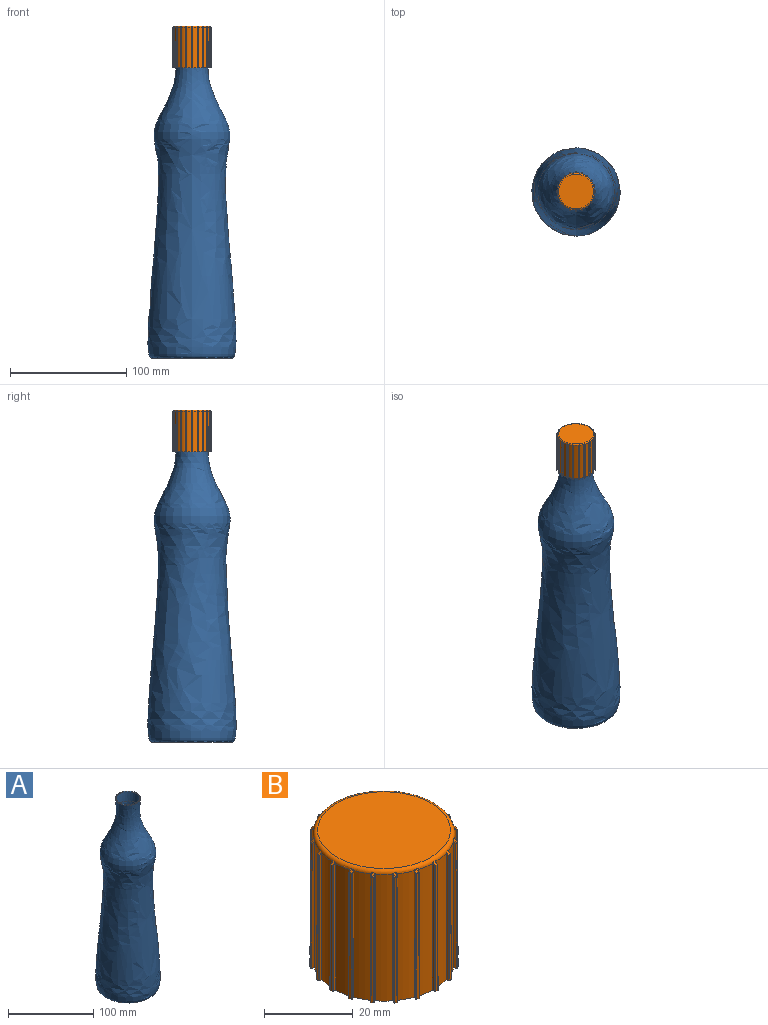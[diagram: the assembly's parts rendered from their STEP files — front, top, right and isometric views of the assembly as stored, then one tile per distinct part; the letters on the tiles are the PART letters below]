
ASSEMBLY  parts=2 mates=1
PART A: 4 faces, bbox 76x76x269.3 mm
  f0: revolved ~269.25x75.99mm, area 54828.4mm2, adj f3
  f1: revolved ~252.83x70.44mm, area 48526.9mm2, adj f2
  f2: cone r=13.64mm half-angle=3.7deg, axis (0,0,1), area 1081.3mm2, adj f1,f3
  f3: plane 29.42x29.42mm, normal (0,0,1), area 95.4mm2, adj f0,f2
PART B: 267 faces, bbox 35.1x35.1x36 mm
  f0: cylinder r=16mm len=35mm, axis (0,0,1), area 140.9mm2, adj f19,f25,f88,f255
  f1: cylinder r=16mm len=35mm, axis (0,0,1), area 140.9mm2, adj f19,f25,f160,f243
  f2: cylinder r=16mm len=35mm, axis (0,0,1), area 140.9mm2, adj f19,f25,f112,f231
  f3: cylinder r=16mm len=35mm, axis (0,0,1), area 140.9mm2, adj f19,f25,f76,f219
  f4: cylinder r=16mm len=35mm, axis (0,0,1), area 140.9mm2, adj f19,f25,f52,f207
  f5: cylinder r=16mm len=35mm, axis (0,0,1), area 140.9mm2, adj f19,f25,f64,f195
  f6: cylinder r=16mm len=35mm, axis (0,0,1), area 140.9mm2, adj f19,f21,f25,f183
  f7: cylinder r=16mm len=35mm, axis (0,0,1), area 140.9mm2, adj f19,f25,f171,f184
  f8: cylinder r=16mm len=35mm, axis (0,0,1), area 140.9mm2, adj f19,f25,f136,f159
  f9: cylinder r=16mm len=35mm, axis (0,0,1), area 140.9mm2, adj f19,f25,f147,f208
  f10: cylinder r=16mm len=35mm, axis (0,0,1), area 140.9mm2, adj f19,f25,f100,f135
  f11: cylinder r=16mm len=35mm, axis (0,0,1), area 140.9mm2, adj f19,f25,f40,f123
  f12: cylinder r=16mm len=35mm, axis (0,0,1), area 140.9mm2, adj f19,f25,f111,f244
  f13: cylinder r=16mm len=35mm, axis (0,0,1), area 140.9mm2, adj f19,f25,f99,f256
  f14: cylinder r=16mm len=35mm, axis (0,0,1), area 140.9mm2, adj f19,f25,f87,f148
  f15: cylinder r=16mm len=35mm, axis (0,0,1), area 140.9mm2, adj f19,f25,f75,f172
  f16: cylinder r=16mm len=35mm, axis (0,0,1), area 140.9mm2, adj f19,f25,f63,f124
  f17: cylinder r=16mm len=35mm, axis (0,0,1), area 140.9mm2, adj f19,f25,f51,f220
  f18: cylinder r=16mm len=35mm, axis (0,0,1), area 140.9mm2, adj f19,f25,f39,f232
  f19: torus R=15mm, axis (0,0,1), area 148.2mm2, adj f0,f1,f2,f3,f4,f5,f6,f7
  f20: plane 35.03x0.66mm, normal (-0.31,-0.95,0), area 21mm2, adj f19,f22,f25,f28,f33
  f21: plane 35.03x0.66mm, normal (0.31,0.95,0), area 21mm2, adj f6,f19,f24,f25,f29
  f22: cylinder r=0.2mm len=0.82mm, axis (-0.67,0.22,-0.71), area 0.3mm2, adj f19,f20,f23,f27,f31
  f23: cylinder r=0.2mm len=0.82mm, axis (-0.31,-0.95,0), area 0.1mm2, adj f19,f22,f24,f27
  f24: cylinder r=0.2mm len=0.84mm, axis (-0.67,0.22,-0.71), area 0.3mm2, adj f19,f21,f23,f27,f32
  f25: plane 33.77x33.77mm, normal (0,0,-1), area 66.9mm2, adj f0,f1,f2,f3,f4,f5,f6,f7
  f26: plane 34.53x0.63mm, normal (-0.95,0.31,0.01), area 20.7mm2, adj f25,f28,f29,f30
  f27: plane 0.76x0.76mm, normal (-0.67,0.22,0.71), area 0.5mm2, adj f22,f23,f24,f30
  f28: cylinder r=0.2mm len=34.53mm, axis (-0.01,0,-1), area 10.8mm2, adj f20,f25,f26,f31
  f29: cylinder r=0.2mm len=34.53mm, axis (0.01,0,1), area 10.8mm2, adj f21,f25,f26,f32
  f30: cylinder r=0.2mm len=0.59mm, axis (-0.31,-0.95,0), area 0.1mm2, adj f26,f27,f31,f32
  f31: sphere r=0.2mm, area 0mm2, adj f22,f28,f30
  f32: sphere r=0.2mm, area 0mm2, adj f24,f29,f30
  f33: cylinder r=16mm len=35mm, axis (0,0,1), area 140.9mm2, adj f19,f20,f25,f196
  f34: plane 30x30mm, normal (0,0,1), area 706.9mm2, adj f19
  f35: plane 27x27mm, normal (0,0,-1), area 572.6mm2, adj f36
  f36: torus R=13.5mm, axis (0,0,1), area 139.5mm2, adj f35,f37
  f37: cylinder r=14.5mm len=32.5mm, axis (0,0,1), area 2961mm2, adj f36,f38
  f38: torus R=15.5mm, axis (0,0,1), area 146.7mm2, adj f25,f37
  f39: plane 35.03x0.56mm, normal (0.81,-0.59,0), area 21mm2, adj f18,f19,f25,f41,f46
  f40: plane 35.03x0.56mm, normal (-0.81,0.59,0), area 21mm2, adj f11,f19,f25,f43,f47
  f41: cylinder r=0.2mm len=0.82mm, axis (-0.42,-0.57,-0.71), area 0.3mm2, adj f19,f39,f42,f45,f49
  f42: cylinder r=0.2mm len=0.73mm, axis (0.81,-0.59,0), area 0.1mm2, adj f19,f41,f43,f45
  f43: cylinder r=0.2mm len=0.82mm, axis (-0.42,-0.57,-0.71), area 0.3mm2, adj f19,f40,f42,f45,f50
  f44: plane 34.53x0.59mm, normal (-0.59,-0.81,0.01), area 20.7mm2, adj f25,f46,f47,f48
  f45: plane 0.84x0.84mm, normal (-0.41,-0.57,0.71), area 0.5mm2, adj f41,f42,f43,f48
  f46: cylinder r=0.2mm len=34.53mm, axis (0,0,-1), area 10.8mm2, adj f25,f39,f44,f49
  f47: cylinder r=0.2mm len=34.53mm, axis (0,0,1), area 10.8mm2, adj f25,f40,f44,f50
  f48: cylinder r=0.2mm len=0.52mm, axis (0.81,-0.59,0), area 0.1mm2, adj f44,f45,f49,f50
  f49: sphere r=0.2mm, area 0mm2, adj f41,f46,f48
  f50: sphere r=0.2mm, area 0mm2, adj f43,f47,f48
  f51: plane 35.03x0.66mm, normal (-0.95,0.31,0), area 21mm2, adj f17,f19,f25,f53,f58
  f52: plane 35.03x0.66mm, normal (0.95,-0.31,0), area 21mm2, adj f4,f19,f25,f55,f59
  f53: cylinder r=0.2mm len=0.82mm, axis (0.22,0.67,-0.71), area 0.3mm2, adj f19,f51,f54,f57,f61
  f54: cylinder r=0.2mm len=0.82mm, axis (-0.95,0.31,0), area 0.1mm2, adj f19,f53,f55,f57
  f55: cylinder r=0.2mm len=0.84mm, axis (0.22,0.67,-0.71), area 0.3mm2, adj f19,f52,f54,f57,f62
  f56: plane 34.53x0.63mm, normal (0.31,0.95,0.01), area 20.7mm2, adj f25,f58,f59,f60
  f57: plane 0.76x0.76mm, normal (0.22,0.67,0.71), area 0.5mm2, adj f53,f54,f55,f60
  f58: cylinder r=0.2mm len=34.53mm, axis (0,0.01,-1), area 10.8mm2, adj f25,f51,f56,f61
  f59: cylinder r=0.2mm len=34.53mm, axis (0,-0.01,1), area 10.8mm2, adj f25,f52,f56,f62
  f60: cylinder r=0.2mm len=0.59mm, axis (-0.95,0.31,0), area 0.1mm2, adj f56,f57,f61,f62
  f61: sphere r=0.2mm, area 0mm2, adj f53,f58,f60
  f62: sphere r=0.2mm, area 0mm2, adj f55,f59,f60
  f63: plane 35.03x0.66mm, normal (0.31,-0.95,0), area 21mm2, adj f16,f19,f25,f65,f70
  f64: plane 35.03x0.66mm, normal (-0.31,0.95,0), area 21mm2, adj f5,f19,f25,f67,f71
  f65: cylinder r=0.2mm len=0.84mm, axis (-0.67,-0.22,-0.71), area 0.3mm2, adj f19,f63,f66,f69,f73
  f66: cylinder r=0.2mm len=0.82mm, axis (0.31,-0.95,0), area 0.1mm2, adj f19,f65,f67,f69
  f67: cylinder r=0.2mm len=0.82mm, axis (-0.67,-0.22,-0.71), area 0.3mm2, adj f19,f64,f66,f69,f74
  f68: plane 34.53x0.63mm, normal (-0.95,-0.31,0.01), area 20.7mm2, adj f25,f70,f71,f72
  f69: plane 0.76x0.76mm, normal (-0.67,-0.22,0.71), area 0.5mm2, adj f65,f66,f67,f72
  f70: cylinder r=0.2mm len=34.53mm, axis (-0.01,0,-1), area 10.8mm2, adj f25,f63,f68,f73
  f71: cylinder r=0.2mm len=34.53mm, axis (0.01,0,1), area 10.8mm2, adj f25,f64,f68,f74
  f72: cylinder r=0.2mm len=0.59mm, axis (0.31,-0.95,0), area 0.1mm2, adj f68,f69,f73,f74
  f73: sphere r=0.2mm, area 0mm2, adj f65,f70,f72
  f74: sphere r=0.2mm, area 0mm2, adj f67,f71,f72
  f75: plane 35.03x0.66mm, normal (-0.95,-0.31,0), area 21mm2, adj f15,f19,f25,f77,f82
  f76: plane 35.03x0.66mm, normal (0.95,0.31,0), area 21mm2, adj f3,f19,f25,f79,f83
  f77: cylinder r=0.2mm len=0.84mm, axis (-0.22,0.67,-0.71), area 0.3mm2, adj f19,f75,f78,f81,f85
  f78: cylinder r=0.2mm len=0.82mm, axis (-0.95,-0.31,0), area 0.1mm2, adj f19,f77,f79,f81
  f79: cylinder r=0.2mm len=0.82mm, axis (-0.22,0.67,-0.71), area 0.3mm2, adj f19,f76,f78,f81,f86
  f80: plane 34.53x0.63mm, normal (-0.31,0.95,0.01), area 20.7mm2, adj f25,f82,f83,f84
  f81: plane 0.76x0.76mm, normal (-0.22,0.67,0.71), area 0.5mm2, adj f77,f78,f79,f84
  f82: cylinder r=0.2mm len=34.53mm, axis (0,0.01,-1), area 10.8mm2, adj f25,f75,f80,f85
  f83: cylinder r=0.2mm len=34.53mm, axis (0,-0.01,1), area 10.8mm2, adj f25,f76,f80,f86
  f84: cylinder r=0.2mm len=0.59mm, axis (-0.95,-0.31,0), area 0.1mm2, adj f80,f81,f85,f86
  f85: sphere r=0.2mm, area 0mm2, adj f77,f82,f84
  f86: sphere r=0.2mm, area 0mm2, adj f79,f83,f84
  f87: plane 35.03x0.66mm, normal (-0.31,0.95,0), area 21mm2, adj f14,f19,f25,f89,f94
  f88: plane 35.03x0.66mm, normal (0.31,-0.95,0), area 21mm2, adj f0,f19,f25,f91,f95
  f89: cylinder r=0.2mm len=0.84mm, axis (0.67,0.22,-0.71), area 0.3mm2, adj f19,f87,f90,f93,f97
  f90: cylinder r=0.2mm len=0.82mm, axis (-0.31,0.95,0), area 0.1mm2, adj f19,f89,f91,f93
  f91: cylinder r=0.2mm len=0.82mm, axis (0.67,0.22,-0.71), area 0.3mm2, adj f19,f88,f90,f93,f98
  f92: plane 34.53x0.63mm, normal (0.95,0.31,0.01), area 20.7mm2, adj f25,f94,f95,f96
  f93: plane 0.76x0.76mm, normal (0.67,0.22,0.71), area 0.5mm2, adj f89,f90,f91,f96
  f94: cylinder r=0.2mm len=34.53mm, axis (0.01,0,-1), area 10.8mm2, adj f25,f87,f92,f97
  f95: cylinder r=0.2mm len=34.53mm, axis (-0.01,0,1), area 10.8mm2, adj f25,f88,f92,f98
  f96: cylinder r=0.2mm len=0.59mm, axis (-0.31,0.95,0), area 0.1mm2, adj f92,f93,f97,f98
  f97: sphere r=0.2mm, area 0mm2, adj f89,f94,f96
  f98: sphere r=0.2mm, area 0mm2, adj f91,f95,f96
  f99: plane 35.03x0.66mm, normal (0.31,0.95,0), area 21mm2, adj f13,f19,f25,f101,f106
  f100: plane 35.03x0.66mm, normal (-0.31,-0.95,0), area 21mm2, adj f10,f19,f25,f103,f107
  f101: cylinder r=0.2mm len=0.82mm, axis (0.67,-0.22,-0.71), area 0.3mm2, adj f19,f99,f102,f105,f109
  f102: cylinder r=0.2mm len=0.82mm, axis (0.31,0.95,0), area 0.1mm2, adj f19,f101,f103,f105
  f103: cylinder r=0.2mm len=0.84mm, axis (0.67,-0.22,-0.71), area 0.3mm2, adj f19,f100,f102,f105,f110
  f104: plane 34.53x0.63mm, normal (0.95,-0.31,0.01), area 20.7mm2, adj f25,f106,f107,f108
  f105: plane 0.76x0.76mm, normal (0.67,-0.22,0.71), area 0.5mm2, adj f101,f102,f103,f108
  f106: cylinder r=0.2mm len=34.53mm, axis (0.01,0,-1), area 10.8mm2, adj f25,f99,f104,f109
  f107: cylinder r=0.2mm len=34.53mm, axis (-0.01,0,1), area 10.8mm2, adj f25,f100,f104,f110
  f108: cylinder r=0.2mm len=0.59mm, axis (0.31,0.95,0), area 0.1mm2, adj f104,f105,f109,f110
  f109: sphere r=0.2mm, area 0mm2, adj f101,f106,f108
  f110: sphere r=0.2mm, area 0mm2, adj f103,f107,f108
  f111: plane 35.03x0.7mm, normal (1,0,0), area 21mm2, adj f12,f19,f25,f113,f118
  f112: plane 35.03x0.7mm, normal (-1,0,0), area 21mm2, adj f2,f19,f25,f115,f119
  f113: cylinder r=0.2mm len=0.82mm, axis (0,-0.71,-0.71), area 0.3mm2, adj f19,f111,f114,f117,f121
  f114: cylinder r=0.2mm len=0.82mm, axis (1,0,0), area 0.1mm2, adj f19,f113,f115,f117
  f115: cylinder r=0.2mm len=0.82mm, axis (0,-0.71,-0.71), area 0.3mm2, adj f19,f112,f114,f117,f122
  f116: plane 34.53x0.6mm, normal (0,-1,0.01), area 20.7mm2, adj f25,f118,f119,f120
  f117: plane 0.6x0.6mm, normal (0,-0.71,0.71), area 0.5mm2, adj f113,f114,f115,f120
  f118: cylinder r=0.2mm len=34.53mm, axis (0,-0.01,-1), area 10.8mm2, adj f25,f111,f116,f121
  f119: cylinder r=0.2mm len=34.53mm, axis (0,0.01,1), area 10.8mm2, adj f25,f112,f116,f122
  f120: cylinder r=0.2mm len=0.6mm, axis (1,0,0), area 0.1mm2, adj f116,f117,f121,f122
  f121: sphere r=0.2mm, area 0mm2, adj f113,f118,f120
  f122: sphere r=0.2mm, area 0mm2, adj f115,f119,f120
  f123: plane 35.03x0.56mm, normal (0.59,-0.81,0), area 21mm2, adj f11,f19,f25,f125,f130
  f124: plane 35.03x0.56mm, normal (-0.59,0.81,0), area 21mm2, adj f16,f19,f25,f127,f131
  f125: cylinder r=0.2mm len=0.82mm, axis (-0.57,-0.42,-0.71), area 0.3mm2, adj f19,f123,f126,f129,f133
  f126: cylinder r=0.2mm len=0.73mm, axis (0.59,-0.81,0), area 0.1mm2, adj f19,f125,f127,f129
  f127: cylinder r=0.2mm len=0.82mm, axis (-0.57,-0.42,-0.71), area 0.3mm2, adj f19,f124,f126,f129,f134
  f128: plane 34.53x0.59mm, normal (-0.81,-0.59,0.01), area 20.7mm2, adj f25,f130,f131,f132
  f129: plane 0.84x0.84mm, normal (-0.57,-0.41,0.71), area 0.5mm2, adj f125,f126,f127,f132
  f130: cylinder r=0.2mm len=34.53mm, axis (0,0,-1), area 10.8mm2, adj f25,f123,f128,f133
  f131: cylinder r=0.2mm len=34.53mm, axis (0,0,1), area 10.8mm2, adj f25,f124,f128,f134
  f132: cylinder r=0.2mm len=0.52mm, axis (0.59,-0.81,0), area 0.1mm2, adj f128,f129,f133,f134
  f133: sphere r=0.2mm, area 0mm2, adj f125,f130,f132
  f134: sphere r=0.2mm, area 0mm2, adj f127,f131,f132
  f135: plane 35.03x0.56mm, normal (0.59,0.81,0), area 21mm2, adj f10,f19,f25,f137,f142
  f136: plane 35.03x0.56mm, normal (-0.59,-0.81,0), area 21mm2, adj f8,f19,f25,f139,f143
  f137: cylinder r=0.2mm len=0.82mm, axis (0.57,-0.42,-0.71), area 0.3mm2, adj f19,f135,f138,f141,f145
  f138: cylinder r=0.2mm len=0.73mm, axis (0.59,0.81,0), area 0.1mm2, adj f19,f137,f139,f141
  f139: cylinder r=0.2mm len=0.82mm, axis (0.57,-0.42,-0.71), area 0.3mm2, adj f19,f136,f138,f141,f146
  f140: plane 34.53x0.59mm, normal (0.81,-0.59,0.01), area 20.7mm2, adj f25,f142,f143,f144
  f141: plane 0.84x0.84mm, normal (0.57,-0.41,0.71), area 0.5mm2, adj f137,f138,f139,f144
  f142: cylinder r=0.2mm len=34.53mm, axis (0,0,-1), area 10.8mm2, adj f25,f135,f140,f145
  f143: cylinder r=0.2mm len=34.53mm, axis (0,0,1), area 10.8mm2, adj f25,f136,f140,f146
  f144: cylinder r=0.2mm len=0.52mm, axis (0.59,0.81,0), area 0.1mm2, adj f140,f141,f145,f146
  f145: sphere r=0.2mm, area 0mm2, adj f137,f142,f144
  f146: sphere r=0.2mm, area 0mm2, adj f139,f143,f144
  f147: plane 35.03x0.56mm, normal (-0.59,0.81,0), area 21mm2, adj f9,f19,f25,f149,f154
  f148: plane 35.03x0.56mm, normal (0.59,-0.81,0), area 21mm2, adj f14,f19,f25,f151,f155
  f149: cylinder r=0.2mm len=0.82mm, axis (0.57,0.42,-0.71), area 0.3mm2, adj f19,f147,f150,f153,f157
  f150: cylinder r=0.2mm len=0.73mm, axis (-0.59,0.81,0), area 0.1mm2, adj f19,f149,f151,f153
  f151: cylinder r=0.2mm len=0.82mm, axis (0.57,0.42,-0.71), area 0.3mm2, adj f19,f148,f150,f153,f158
  f152: plane 34.53x0.59mm, normal (0.81,0.59,0.01), area 20.7mm2, adj f25,f154,f155,f156
  f153: plane 0.84x0.84mm, normal (0.57,0.41,0.71), area 0.5mm2, adj f149,f150,f151,f156
  f154: cylinder r=0.2mm len=34.53mm, axis (0,0,-1), area 10.8mm2, adj f25,f147,f152,f157
  f155: cylinder r=0.2mm len=34.53mm, axis (0,0,1), area 10.8mm2, adj f25,f148,f152,f158
  f156: cylinder r=0.2mm len=0.52mm, axis (-0.59,0.81,0), area 0.1mm2, adj f152,f153,f157,f158
  f157: sphere r=0.2mm, area 0mm2, adj f149,f154,f156
  f158: sphere r=0.2mm, area 0mm2, adj f151,f155,f156
  f159: plane 35.03x0.56mm, normal (0.81,0.59,0), area 21mm2, adj f8,f19,f25,f161,f166
  f160: plane 35.03x0.56mm, normal (-0.81,-0.59,0), area 21mm2, adj f1,f19,f25,f163,f167
  f161: cylinder r=0.2mm len=0.82mm, axis (0.42,-0.57,-0.71), area 0.3mm2, adj f19,f159,f162,f165,f169
  f162: cylinder r=0.2mm len=0.73mm, axis (0.81,0.59,0), area 0.1mm2, adj f19,f161,f163,f165
  f163: cylinder r=0.2mm len=0.82mm, axis (0.42,-0.57,-0.71), area 0.3mm2, adj f19,f160,f162,f165,f170
  f164: plane 34.53x0.59mm, normal (0.59,-0.81,0.01), area 20.7mm2, adj f25,f166,f167,f168
  f165: plane 0.84x0.84mm, normal (0.41,-0.57,0.71), area 0.5mm2, adj f161,f162,f163,f168
  f166: cylinder r=0.2mm len=34.53mm, axis (0,0,-1), area 10.8mm2, adj f25,f159,f164,f169
  f167: cylinder r=0.2mm len=34.53mm, axis (0,0,1), area 10.8mm2, adj f25,f160,f164,f170
  f168: cylinder r=0.2mm len=0.52mm, axis (0.81,0.59,0), area 0.1mm2, adj f164,f165,f169,f170
  f169: sphere r=0.2mm, area 0mm2, adj f161,f166,f168
  f170: sphere r=0.2mm, area 0mm2, adj f163,f167,f168
  f171: plane 35.03x0.56mm, normal (-0.81,-0.59,0), area 21mm2, adj f7,f19,f25,f173,f178
  f172: plane 35.03x0.56mm, normal (0.81,0.59,0), area 21mm2, adj f15,f19,f25,f175,f179
  f173: cylinder r=0.2mm len=0.82mm, axis (-0.42,0.57,-0.71), area 0.3mm2, adj f19,f171,f174,f177,f181
  f174: cylinder r=0.2mm len=0.73mm, axis (-0.81,-0.59,0), area 0.1mm2, adj f19,f173,f175,f177
  f175: cylinder r=0.2mm len=0.82mm, axis (-0.42,0.57,-0.71), area 0.3mm2, adj f19,f172,f174,f177,f182
  f176: plane 34.53x0.59mm, normal (-0.59,0.81,0.01), area 20.7mm2, adj f25,f178,f179,f180
  f177: plane 0.84x0.84mm, normal (-0.41,0.57,0.71), area 0.5mm2, adj f173,f174,f175,f180
  f178: cylinder r=0.2mm len=34.53mm, axis (0,0,-1), area 10.8mm2, adj f25,f171,f176,f181
  f179: cylinder r=0.2mm len=34.53mm, axis (0,0,1), area 10.8mm2, adj f25,f172,f176,f182
  f180: cylinder r=0.2mm len=0.52mm, axis (-0.81,-0.59,0), area 0.1mm2, adj f176,f177,f181,f182
  f181: sphere r=0.2mm, area 0mm2, adj f173,f178,f180
  f182: sphere r=0.2mm, area 0mm2, adj f175,f179,f180
  f183: plane 35.03x0.56mm, normal (-0.59,-0.81,0), area 21mm2, adj f6,f19,f25,f185,f190
  f184: plane 35.03x0.56mm, normal (0.59,0.81,0), area 21mm2, adj f7,f19,f25,f187,f191
  f185: cylinder r=0.2mm len=0.82mm, axis (-0.57,0.42,-0.71), area 0.3mm2, adj f19,f183,f186,f189,f193
  f186: cylinder r=0.2mm len=0.73mm, axis (-0.59,-0.81,0), area 0.1mm2, adj f19,f185,f187,f189
  f187: cylinder r=0.2mm len=0.82mm, axis (-0.57,0.42,-0.71), area 0.3mm2, adj f19,f184,f186,f189,f194
  f188: plane 34.53x0.59mm, normal (-0.81,0.59,0.01), area 20.7mm2, adj f25,f190,f191,f192
  f189: plane 0.84x0.84mm, normal (-0.57,0.41,0.71), area 0.5mm2, adj f185,f186,f187,f192
  f190: cylinder r=0.2mm len=34.53mm, axis (0,0,-1), area 10.8mm2, adj f25,f183,f188,f193
  f191: cylinder r=0.2mm len=34.53mm, axis (0,0,1), area 10.8mm2, adj f25,f184,f188,f194
  f192: cylinder r=0.2mm len=0.52mm, axis (-0.59,-0.81,0), area 0.1mm2, adj f188,f189,f193,f194
  f193: sphere r=0.2mm, area 0mm2, adj f185,f190,f192
  f194: sphere r=0.2mm, area 0mm2, adj f187,f191,f192
  f195: plane 35.03x0.7mm, normal (0,-1,0), area 21mm2, adj f5,f19,f25,f197,f202
  f196: plane 35.03x0.7mm, normal (0,1,0), area 21mm2, adj f19,f25,f33,f199,f203
  f197: cylinder r=0.2mm len=0.82mm, axis (-0.71,0,-0.71), area 0.3mm2, adj f19,f195,f198,f201,f205
  f198: cylinder r=0.2mm len=0.82mm, axis (0,-1,0), area 0.1mm2, adj f19,f197,f199,f201
  f199: cylinder r=0.2mm len=0.82mm, axis (-0.71,0,-0.71), area 0.3mm2, adj f19,f196,f198,f201,f206
  f200: plane 34.53x0.6mm, normal (-1,0,0.01), area 20.7mm2, adj f25,f202,f203,f204
  f201: plane 0.6x0.6mm, normal (-0.71,0,0.71), area 0.5mm2, adj f197,f198,f199,f204
  f202: cylinder r=0.2mm len=34.53mm, axis (-0.01,0,-1), area 10.8mm2, adj f25,f195,f200,f205
  f203: cylinder r=0.2mm len=34.53mm, axis (0.01,0,1), area 10.8mm2, adj f25,f196,f200,f206
  f204: cylinder r=0.2mm len=0.6mm, axis (0,-1,0), area 0.1mm2, adj f200,f201,f205,f206
  f205: sphere r=0.2mm, area 0mm2, adj f197,f202,f204
  f206: sphere r=0.2mm, area 0mm2, adj f199,f203,f204
  f207: plane 35.03x0.56mm, normal (-0.81,0.59,0), area 21mm2, adj f4,f19,f25,f209,f214
  f208: plane 35.03x0.56mm, normal (0.81,-0.59,0), area 21mm2, adj f9,f19,f25,f211,f215
  f209: cylinder r=0.2mm len=0.82mm, axis (0.42,0.57,-0.71), area 0.3mm2, adj f19,f207,f210,f213,f217
  f210: cylinder r=0.2mm len=0.73mm, axis (-0.81,0.59,0), area 0.1mm2, adj f19,f209,f211,f213
  f211: cylinder r=0.2mm len=0.82mm, axis (0.42,0.57,-0.71), area 0.3mm2, adj f19,f208,f210,f213,f218
  f212: plane 34.53x0.59mm, normal (0.59,0.81,0.01), area 20.7mm2, adj f25,f214,f215,f216
  f213: plane 0.84x0.84mm, normal (0.41,0.57,0.71), area 0.5mm2, adj f209,f210,f211,f216
  f214: cylinder r=0.2mm len=34.53mm, axis (0,0,-1), area 10.8mm2, adj f25,f207,f212,f217
  f215: cylinder r=0.2mm len=34.53mm, axis (0,0,1), area 10.8mm2, adj f25,f208,f212,f218
  f216: cylinder r=0.2mm len=0.52mm, axis (-0.81,0.59,0), area 0.1mm2, adj f212,f213,f217,f218
  f217: sphere r=0.2mm, area 0mm2, adj f209,f214,f216
  f218: sphere r=0.2mm, area 0mm2, adj f211,f215,f216
  f219: plane 35.03x0.7mm, normal (-1,0,0), area 21mm2, adj f3,f19,f25,f221,f226
  f220: plane 35.03x0.7mm, normal (1,0,0), area 21mm2, adj f17,f19,f25,f223,f227
  f221: cylinder r=0.2mm len=0.82mm, axis (0,0.71,-0.71), area 0.3mm2, adj f19,f219,f222,f225,f229
  f222: cylinder r=0.2mm len=0.82mm, axis (-1,0,0), area 0.1mm2, adj f19,f221,f223,f225
  f223: cylinder r=0.2mm len=0.82mm, axis (0,0.71,-0.71), area 0.3mm2, adj f19,f220,f222,f225,f230
  f224: plane 34.53x0.6mm, normal (0,1,0.01), area 20.7mm2, adj f25,f226,f227,f228
  f225: plane 0.6x0.6mm, normal (0,0.71,0.71), area 0.5mm2, adj f221,f222,f223,f228
  f226: cylinder r=0.2mm len=34.53mm, axis (0,0.01,-1), area 10.8mm2, adj f25,f219,f224,f229
  f227: cylinder r=0.2mm len=34.53mm, axis (0,-0.01,1), area 10.8mm2, adj f25,f220,f224,f230
  f228: cylinder r=0.2mm len=0.6mm, axis (-1,0,0), area 0.1mm2, adj f224,f225,f229,f230
  f229: sphere r=0.2mm, area 0mm2, adj f221,f226,f228
  f230: sphere r=0.2mm, area 0mm2, adj f223,f227,f228
  f231: plane 35.03x0.66mm, normal (0.95,-0.31,0), area 21mm2, adj f2,f19,f25,f233,f238
  f232: plane 35.03x0.66mm, normal (-0.95,0.31,0), area 21mm2, adj f18,f19,f25,f235,f239
  f233: cylinder r=0.2mm len=0.82mm, axis (-0.22,-0.67,-0.71), area 0.3mm2, adj f19,f231,f234,f237,f241
  f234: cylinder r=0.2mm len=0.82mm, axis (0.95,-0.31,0), area 0.1mm2, adj f19,f233,f235,f237
  f235: cylinder r=0.2mm len=0.84mm, axis (-0.22,-0.67,-0.71), area 0.3mm2, adj f19,f232,f234,f237,f242
  f236: plane 34.53x0.63mm, normal (-0.31,-0.95,0.01), area 20.7mm2, adj f25,f238,f239,f240
  f237: plane 0.76x0.76mm, normal (-0.22,-0.67,0.71), area 0.5mm2, adj f233,f234,f235,f240
  f238: cylinder r=0.2mm len=34.53mm, axis (0,-0.01,-1), area 10.8mm2, adj f25,f231,f236,f241
  f239: cylinder r=0.2mm len=34.53mm, axis (0,0.01,1), area 10.8mm2, adj f25,f232,f236,f242
  f240: cylinder r=0.2mm len=0.59mm, axis (0.95,-0.31,0), area 0.1mm2, adj f236,f237,f241,f242
  f241: sphere r=0.2mm, area 0mm2, adj f233,f238,f240
  f242: sphere r=0.2mm, area 0mm2, adj f235,f239,f240
  f243: plane 35.03x0.66mm, normal (0.95,0.31,0), area 21mm2, adj f1,f19,f25,f245,f250
  f244: plane 35.03x0.66mm, normal (-0.95,-0.31,0), area 21mm2, adj f12,f19,f25,f247,f251
  f245: cylinder r=0.2mm len=0.84mm, axis (0.22,-0.67,-0.71), area 0.3mm2, adj f19,f243,f246,f249,f253
  f246: cylinder r=0.2mm len=0.82mm, axis (0.95,0.31,0), area 0.1mm2, adj f19,f245,f247,f249
  f247: cylinder r=0.2mm len=0.82mm, axis (0.22,-0.67,-0.71), area 0.3mm2, adj f19,f244,f246,f249,f254
  f248: plane 34.53x0.63mm, normal (0.31,-0.95,0.01), area 20.7mm2, adj f25,f250,f251,f252
  f249: plane 0.76x0.76mm, normal (0.22,-0.67,0.71), area 0.5mm2, adj f245,f246,f247,f252
  f250: cylinder r=0.2mm len=34.53mm, axis (0,-0.01,-1), area 10.8mm2, adj f25,f243,f248,f253
  f251: cylinder r=0.2mm len=34.53mm, axis (0,0.01,1), area 10.8mm2, adj f25,f244,f248,f254
  f252: cylinder r=0.2mm len=0.59mm, axis (0.95,0.31,0), area 0.1mm2, adj f248,f249,f253,f254
  f253: sphere r=0.2mm, area 0mm2, adj f245,f250,f252
  f254: sphere r=0.2mm, area 0mm2, adj f247,f251,f252
  f255: plane 35.03x0.7mm, normal (0,1,0), area 21mm2, adj f0,f19,f25,f257,f262
  f256: plane 35.03x0.7mm, normal (0,-1,0), area 21mm2, adj f13,f19,f25,f259,f263
  f257: cylinder r=0.2mm len=0.82mm, axis (0.71,0,-0.71), area 0.3mm2, adj f19,f255,f258,f261,f265
  f258: cylinder r=0.2mm len=0.82mm, axis (0,1,0), area 0.1mm2, adj f19,f257,f259,f261
  f259: cylinder r=0.2mm len=0.82mm, axis (0.71,0,-0.71), area 0.3mm2, adj f19,f256,f258,f261,f266
  f260: plane 34.53x0.6mm, normal (1,0,0.01), area 20.7mm2, adj f25,f262,f263,f264
  f261: plane 0.6x0.6mm, normal (0.71,0,0.71), area 0.5mm2, adj f257,f258,f259,f264
  f262: cylinder r=0.2mm len=34.53mm, axis (0.01,0,-1), area 10.8mm2, adj f25,f255,f260,f265
  f263: cylinder r=0.2mm len=34.53mm, axis (-0.01,0,1), area 10.8mm2, adj f25,f256,f260,f266
  f264: cylinder r=0.2mm len=0.6mm, axis (0,1,0), area 0.1mm2, adj f260,f261,f265,f266
  f265: sphere r=0.2mm, area 0mm2, adj f257,f262,f264
  f266: sphere r=0.2mm, area 0mm2, adj f259,f263,f264
PLACE A t=(67.1,69.82,-108.43)mm
PLACE B t=(67.1,69.82,15)mm
MATE fastened B.f0 <-> A.f2  axis (0,0,-1) through (67.1,69.82,49.5)mm
